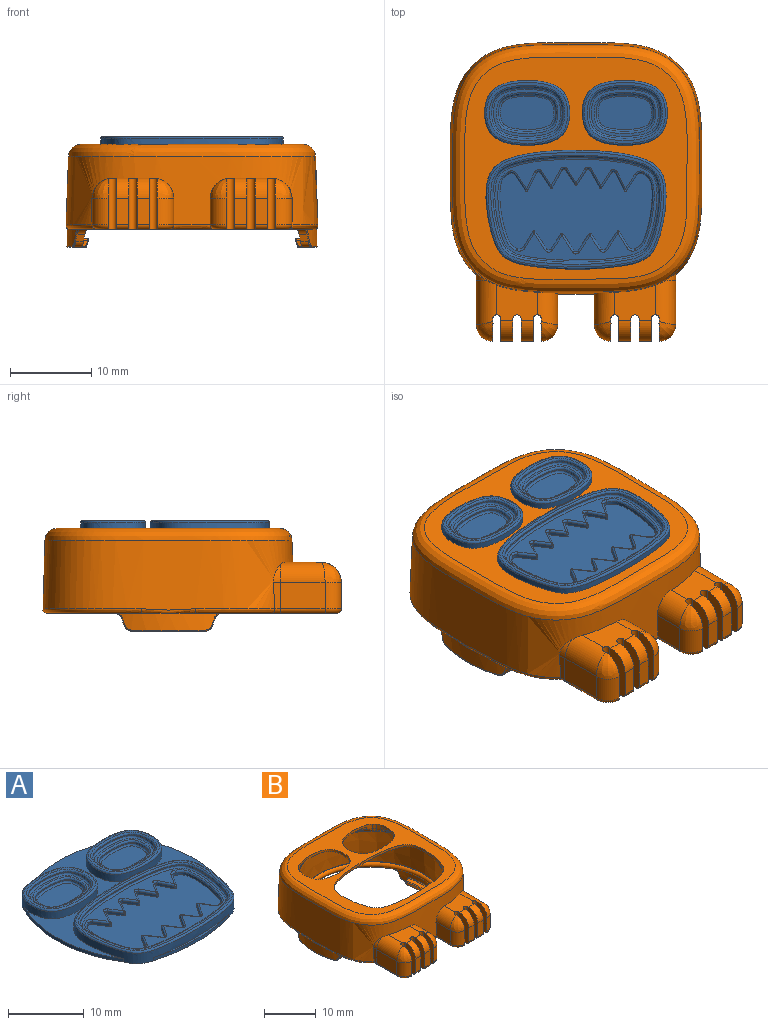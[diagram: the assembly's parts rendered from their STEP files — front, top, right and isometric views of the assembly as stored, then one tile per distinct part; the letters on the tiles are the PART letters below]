
ASSEMBLY  parts=2 mates=1
PART A: 119 faces, bbox 25.6x25.6x2.2 mm
  f0: plane 21.64x14.15mm, normal (0,0,1), area 21.1mm2, adj f114,f116
  f1: plane 9.97x7.48mm, normal (0,0,1), area 9.6mm2, adj f27,f29
  f2: plane 9.97x7.48mm, normal (0,0,1), area 9.6mm2, adj f25,f30
  f3: cylinder r=17.94mm len=17.52mm, axis (0,0,-1), area 9.2mm2, adj f6,f7,f8,f12
  f4: cylinder r=17.8mm len=18mm, axis (0,0,-1), area 9.4mm2, adj f6,f7,f11,f12
  f5: cylinder r=17.94mm len=17.52mm, axis (0,0,-1), area 9.2mm2, adj f6,f7,f8,f11
  f6: plane 25.63x22.38mm, normal (0,0,1), area 121.4mm2, adj f3,f4,f5,f8,f11,f12
  f7: plane 25.63x25.59mm, normal (0,0,-1), area 546.4mm2, adj f3,f4,f5,f8,f9,f11,f12,f117
  f8: extruded ~22.13x14.64mm, area 79.2mm2, adj f3,f5,f6,f7,f9,f10,f116
  f9: cylinder r=24.02mm len=14.06mm, axis (0,0,-1), area 7.1mm2, adj f7,f8,f10
  f10: plane 14.76x1.4mm, normal (0,0,1), area 3.3mm2, adj f8,f9
  f11: extruded ~10.45x7.96mm, area 37.8mm2, adj f4,f5,f6,f7,f29
  f12: extruded ~10.46x7.97mm, area 37.7mm2, adj f3,f4,f6,f7,f30
  f13: extruded ~8.77x6.28mm, area 3.7mm2, adj f25,f26
  f14: plane 8.27x5.78mm, normal (0,0,1), area 7.8mm2, adj f21,f26
  f15: extruded ~8.77x6.28mm, area 3.7mm2, adj f27,f28
  f16: plane 8.27x5.78mm, normal (0,0,1), area 7.8mm2, adj f22,f28
  f17: extruded ~7.07x4.58mm, area 2.9mm2, adj f22,f24
  f18: plane 6.57x4.08mm, normal (0,0,1), area 23.2mm2, adj f24
  f19: extruded ~7.07x4.58mm, area 2.9mm2, adj f21,f23
  f20: plane 6.57x4.08mm, normal (0,0,1), area 23.2mm2, adj f23
  f21: bspline ~7.57x5.09mm, area 7.9mm2, adj f14,f19
  f22: bspline ~7.57x5.09mm, area 7.9mm2, adj f16,f17
  f23: bspline ~7.07x4.59mm, area 7.5mm2, adj f19,f20
  f24: bspline ~7.07x4.59mm, area 7.5mm2, adj f17,f18
  f25: bspline ~9.27x6.78mm, area 10mm2, adj f2,f13
  f26: bspline ~8.77x6.29mm, area 9.6mm2, adj f13,f14
  f27: bspline ~9.27x6.78mm, area 10mm2, adj f1,f15
  f28: bspline ~8.77x6.29mm, area 9.6mm2, adj f15,f16
  f29: bspline ~10.47x7.98mm, area 11.6mm2, adj f1,f11
  f30: bspline ~10.47x7.98mm, area 11.6mm2, adj f2,f12
  f31: extruded ~20.4x12.91mm, area 8.6mm2, adj f114,f115
  f32: plane 19.94x12.45mm, normal (0,0,1), area 60.1mm2, adj f75,f76,f77,f78,f79,f80,f82,f83
  f33: plane 18.75x10.19mm, normal (0,0,1), area 141mm2, adj f34,f35,f36,f37,f38,f39,f40,f41
  f34: cylinder r=0.15mm len=0.4mm, axis (0,0,1), area 0.1mm2, adj f33,f35,f73,f102
  f35: plane 1.92x1.29mm, normal (-0.83,0.56,0), area 0.9mm2, adj f33,f34,f36,f104
  f36: cylinder r=0.25mm len=0.41mm, axis (0,0,1), area 0.2mm2, adj f33,f35,f37,f106
  f37: plane 2.21x1.5mm, normal (0.83,0.56,0), area 1.1mm2, adj f33,f36,f38,f108
  f38: cylinder r=0.15mm len=0.4mm, axis (0,0,1), area 0.1mm2, adj f33,f37,f39,f110
  f39: plane 1.89x1.14mm, normal (-0.86,0.52,0), area 0.9mm2, adj f33,f38,f41,f112
  f40: extruded ~9.27x2.15mm, area 4.1mm2, adj f33,f41,f42,f111
  f41: cylinder r=0.69mm len=0.78mm, axis (0,0,1), area 0.4mm2, adj f33,f39,f40,f113
  f42: cylinder r=0.5mm len=0.64mm, axis (0,0,1), area 0.3mm2, adj f33,f40,f43,f109
  f43: plane 1.98x1.32mm, normal (-0.83,-0.55,0), area 1mm2, adj f33,f42,f44,f107
  f44: cylinder r=0.15mm len=0.4mm, axis (0,0,1), area 0.1mm2, adj f33,f43,f45,f105
  f45: plane 2.23x1.11mm, normal (0.89,-0.45,0), area 1mm2, adj f33,f44,f46,f103
  f46: cylinder r=0.25mm len=0.43mm, axis (0,0,1), area 0.2mm2, adj f33,f45,f47,f101
  f47: plane 1.89x1.23mm, normal (-0.84,-0.55,0), area 0.9mm2, adj f33,f46,f48,f99
  f48: cylinder r=0.15mm len=0.4mm, axis (0,0,1), area 0.1mm2, adj f33,f47,f49,f97
  f49: plane 2.17x1.2mm, normal (0.88,-0.48,0), area 1mm2, adj f33,f48,f50,f95
  f50: cylinder r=0.25mm len=0.43mm, axis (0,0,1), area 0.2mm2, adj f33,f49,f51,f93
  f51: plane 1.81x1.16mm, normal (-0.84,-0.54,0), area 0.9mm2, adj f33,f50,f52,f91
  f52: cylinder r=0.15mm len=0.4mm, axis (0,0,1), area 0.1mm2, adj f33,f51,f53,f89
  f53: plane 1.81x1.16mm, normal (0.84,-0.54,0), area 0.9mm2, adj f33,f52,f54,f87
  f54: cylinder r=0.25mm len=0.43mm, axis (0,0,1), area 0.2mm2, adj f33,f53,f55,f85
  f55: plane 2.17x1.2mm, normal (-0.88,-0.48,0), area 1mm2, adj f33,f54,f56,f83
  f56: cylinder r=0.15mm len=0.4mm, axis (0,0,1), area 0.1mm2, adj f33,f55,f57,f81
  f57: plane 1.89x1.23mm, normal (0.84,-0.55,0), area 0.9mm2, adj f33,f56,f58,f79
  f58: cylinder r=0.25mm len=0.43mm, axis (0,0,1), area 0.2mm2, adj f33,f57,f59,f77
  f59: plane 2.23x1.11mm, normal (-0.89,-0.45,0), area 1mm2, adj f33,f58,f60,f75
  f60: cylinder r=0.15mm len=0.4mm, axis (0,0,1), area 0.1mm2, adj f33,f59,f61,f74
  f61: plane 1.97x1.31mm, normal (0.83,-0.55,0), area 0.9mm2, adj f33,f60,f63,f76
  f62: extruded ~9.26x2.15mm, area 4.1mm2, adj f33,f63,f64,f80
  f63: cylinder r=0.52mm len=0.67mm, axis (0,0,1), area 0.3mm2, adj f33,f61,f62,f78
  f64: cylinder r=0.69mm len=0.78mm, axis (0,0,1), area 0.4mm2, adj f33,f62,f65,f82
  f65: plane 1.89x1.14mm, normal (0.86,0.52,0), area 0.9mm2, adj f33,f64,f66,f84
  f66: cylinder r=0.15mm len=0.4mm, axis (0,0,1), area 0.1mm2, adj f33,f65,f67,f86
  f67: plane 2.21x1.5mm, normal (-0.83,0.56,0), area 1.1mm2, adj f33,f66,f68,f88
  f68: cylinder r=0.25mm len=0.41mm, axis (0,0,1), area 0.2mm2, adj f33,f67,f69,f90
  f69: plane 1.92x1.29mm, normal (0.83,0.56,0), area 0.9mm2, adj f33,f68,f70,f92
  f70: cylinder r=0.15mm len=0.4mm, axis (0,0,1), area 0.1mm2, adj f33,f69,f71,f94
  f71: plane 2.15x1.43mm, normal (-0.83,0.55,0), area 1mm2, adj f33,f70,f72,f96
  f72: cylinder r=0.21mm len=0.4mm, axis (0,0,1), area 0.2mm2, adj f33,f71,f73,f98
  f73: plane 2.15x1.43mm, normal (0.83,0.55,0), area 1mm2, adj f33,f34,f72,f100
  f74: bspline ~0.5x0.27mm, area 0.1mm2, adj f60,f75,f76
  f75: cylinder r=0.25mm len=2.34mm, axis (0.45,-0.89,0), area 0.9mm2, adj f32,f59,f74,f77
  f76: cylinder r=0.25mm len=2.11mm, axis (0.55,0.83,0), area 0.9mm2, adj f32,f61,f74,f78
  f77: torus R=0.5mm, axis (0,0,1), area 0.3mm2, adj f32,f58,f75,f79
  f78: torus R=0.77mm, axis (0,0,1), area 0.3mm2, adj f32,f63,f76,f80
  f79: cylinder r=0.25mm len=2.02mm, axis (0.55,0.84,0), area 0.9mm2, adj f32,f57,f77,f81
  f80: bspline ~10.14x2.62mm, area 4.1mm2, adj f32,f62,f78,f82
  f81: bspline ~0.49x0.27mm, area 0.1mm2, adj f56,f79,f83
  f82: torus R=0.94mm, axis (0,0,1), area 0.4mm2, adj f32,f64,f80,f84
  f83: cylinder r=0.25mm len=2.29mm, axis (0.48,-0.88,0), area 0.9mm2, adj f32,f55,f81,f85
  f84: cylinder r=0.25mm len=2.02mm, axis (-0.52,0.86,0), area 0.8mm2, adj f32,f65,f82,f86
  f85: torus R=0.5mm, axis (0,0,1), area 0.3mm2, adj f32,f54,f83,f87
  f86: bspline ~0.46x0.27mm, area 0.1mm2, adj f66,f84,f88
  f87: cylinder r=0.25mm len=1.94mm, axis (0.54,0.84,0), area 0.8mm2, adj f32,f53,f85,f89
  f88: cylinder r=0.25mm len=2.35mm, axis (-0.56,-0.83,0), area 1mm2, adj f32,f67,f86,f90
  f89: bspline ~0.46x0.27mm, area 0.1mm2, adj f52,f87,f91
  f90: torus R=0.5mm, axis (0,0,1), area 0.3mm2, adj f32,f68,f88,f92
  f91: cylinder r=0.25mm len=1.94mm, axis (0.54,-0.84,0), area 0.8mm2, adj f32,f51,f89,f93
  f92: cylinder r=0.25mm len=2.06mm, axis (-0.56,0.83,0), area 0.9mm2, adj f32,f69,f90,f94
  f93: torus R=0.5mm, axis (0,0,1), area 0.3mm2, adj f32,f50,f91,f95
  f94: bspline ~0.45x0.27mm, area 0.1mm2, adj f70,f92,f96
  f95: cylinder r=0.25mm len=2.29mm, axis (0.48,0.88,0), area 0.9mm2, adj f32,f49,f93,f97
  f96: cylinder r=0.25mm len=2.29mm, axis (-0.55,-0.83,0), area 1mm2, adj f32,f71,f94,f98
  f97: bspline ~0.49x0.27mm, area 0.1mm2, adj f48,f95,f99
  f98: torus R=0.46mm, axis (0,0,1), area 0.2mm2, adj f32,f72,f96,f100
  f99: cylinder r=0.25mm len=2.02mm, axis (0.55,-0.84,0), area 0.9mm2, adj f32,f47,f97,f101
  f100: cylinder r=0.25mm len=2.29mm, axis (-0.55,0.83,0), area 1mm2, adj f32,f73,f98,f102
  f101: torus R=0.5mm, axis (0,0,1), area 0.3mm2, adj f32,f46,f99,f103
  f102: bspline ~0.45x0.27mm, area 0.1mm2, adj f34,f100,f104
  f103: cylinder r=0.25mm len=2.34mm, axis (0.45,0.89,0), area 0.9mm2, adj f32,f45,f101,f105
  f104: cylinder r=0.25mm len=2.06mm, axis (-0.56,-0.83,0), area 0.9mm2, adj f32,f35,f102,f106
  f105: bspline ~0.5x0.27mm, area 0.1mm2, adj f44,f103,f107
  f106: torus R=0.5mm, axis (0,0,1), area 0.3mm2, adj f32,f36,f104,f108
  f107: cylinder r=0.25mm len=2.12mm, axis (0.55,-0.83,0), area 0.9mm2, adj f32,f43,f105,f109
  f108: cylinder r=0.25mm len=2.35mm, axis (-0.56,0.83,0), area 1mm2, adj f32,f37,f106,f110
  f109: torus R=0.75mm, axis (0,0,1), area 0.3mm2, adj f32,f42,f107,f111
  f110: bspline ~0.46x0.27mm, area 0.1mm2, adj f38,f108,f112
  f111: bspline ~10.15x2.61mm, area 4.2mm2, adj f32,f40,f109,f113
  f112: cylinder r=0.25mm len=2.02mm, axis (-0.52,-0.86,0), area 0.8mm2, adj f32,f39,f110,f113
  f113: torus R=0.94mm, axis (0,0,1), area 0.4mm2, adj f32,f41,f111,f112
  f114: bspline ~20.94x13.45mm, area 22.7mm2, adj f0,f31
  f115: bspline ~20.44x12.95mm, area 22.3mm2, adj f31,f32
  f116: bspline ~22.14x14.65mm, area 24.4mm2, adj f0,f8
  f117: cone r=1.05mm half-angle=2deg, axis (0,0,1), area 1.3mm2, adj f7,f118
  f118: plane 2.09x2.09mm, normal (0,0,-1), area 3.4mm2, adj f117
PART B: 284 faces, bbox 35.3x39.1x19.3 mm
  f0: plane 30.01x17.46mm, normal (0,0,-1), area 97.2mm2, adj f13,f14,f15,f18,f19,f29,f37,f40
  f1: plane 5.21x4.6mm, normal (0,0,1), area 17.8mm2, adj f8,f9,f11,f17,f156,f230,f231,f232
  f2: plane 3.25x1.5mm, normal (0,-1,0), area 4.9mm2, adj f8,f13,f231,f235
  f3: plane 3.25x1.5mm, normal (0,-1,0), area 4.9mm2, adj f9,f14,f232,f237
  f4: plane 5.19x4.58mm, normal (0,0,1), area 17.8mm2, adj f12,f17,f158,f160,f162,f220,f221,f223
  f5: plane 3.25x1.5mm, normal (0,-1,0), area 4.9mm2, adj f160,f174,f225,f227
  f6: plane 3.25x1.5mm, normal (0,-1,0), area 4.9mm2, adj f12,f15,f220,f224
  f7: bspline ~2.64x2.42mm, area 5.1mm2, adj f152,f156,f234
  f8: cylinder r=2.5mm len=2.5mm, axis (1,0,0), area 5.9mm2, adj f1,f2,f231,f235
  f9: cylinder r=2.5mm len=2.5mm, axis (1,0,0), area 5.9mm2, adj f1,f3,f232,f237
  f10: bspline ~2.64x2.42mm, area 5.1mm2, adj f11,f153,f229
  f11: cylinder r=2.5mm len=5.49mm, axis (0,-1,0), area 19.9mm2, adj f1,f10,f17,f148,f157,f229,f230
  f12: cylinder r=2.5mm len=2.5mm, axis (1,0,0), area 5.9mm2, adj f4,f6,f220,f224
  f13: cylinder r=0.5mm len=1.5mm, axis (1,0,0), area 1.2mm2, adj f0,f2,f231,f235
  f14: cylinder r=0.5mm len=1.5mm, axis (1,0,0), area 1.2mm2, adj f0,f3,f232,f237
  f15: cylinder r=0.5mm len=1.5mm, axis (1,0,0), area 1.2mm2, adj f0,f6,f220,f224
  f16: plane 30.01x11.69mm, normal (0,0,-1), area 44.9mm2, adj f18,f19,f29,f36,f41,f175,f188,f189
  f17: bspline ~30.97x30.97mm, area 781mm2, adj f1,f4,f11,f146,f147,f149,f150,f156
  f18: cone r=15.12mm half-angle=2deg, axis (0,0,-1), area 23.5mm2, adj f0,f16,f173,f182,f183,f184,f185,f186
  f19: cone r=15.12mm half-angle=2deg, axis (0,0,-1), area 23.5mm2, adj f0,f16,f177,f189,f190,f191,f192,f193
  f20: plane 13.19x2.44mm, normal (0,0,-1), area 4.6mm2, adj f102,f113
  f21: plane 13.37x1.8mm, normal (0,0,-1), area 4.6mm2, adj f103,f114
  f22: plane 13.19x2.44mm, normal (0,0,-1), area 4.6mm2, adj f100,f115
  f23: plane 10.51x1.08mm, normal (0,0,-1), area 3.6mm2, adj f101,f107
  f24: extruded ~10.44x7.96mm, area 17.2mm2, adj f28,f95,f96,f102,f103,f111,f112,f113
  f25: extruded ~10.44x7.96mm, area 17.2mm2, adj f28,f95,f97,f100,f103,f108,f114,f115
  f26: extruded ~22.12x13.12mm, area 25.1mm2, adj f28,f95,f98,f99,f100,f102,f109,f110
  f27: extruded ~17.62x1.72mm, area 11.5mm2, adj f28,f95,f98,f99,f101,f104,f105,f106
  f28: plane 27.38x27.38mm, normal (0,0,1), area 268.4mm2, adj f24,f25,f26,f27,f96,f97,f98,f99
  f29: cone r=14.12mm half-angle=2deg, axis (0,0,-1), area 59.9mm2, adj f0,f16,f30,f31,f32,f33,f34,f35
  f30: plane 1.15x0.94mm, normal (0,-0.94,-0.34), area 1mm2, adj f29,f40,f42,f183
  f31: plane 1.15x0.94mm, normal (0,0.94,-0.34), area 1mm2, adj f29,f41,f43,f187
  f32: plane 9x1.6mm, normal (0,0,-1), area 7.6mm2, adj f29,f42,f43,f45,f62,f85,f185
  f33: plane 1.15x0.94mm, normal (0,-0.94,-0.34), area 1mm2, adj f29,f37,f39,f194
  f34: plane 1.15x0.94mm, normal (0,0.94,-0.34), area 1mm2, adj f29,f36,f38,f190
  f35: plane 9x1.6mm, normal (0,0,-1), area 7.6mm2, adj f29,f38,f39,f51,f67,f84,f192
  f36: cylinder r=1mm len=1.46mm, axis (1,0,0), area 1.2mm2, adj f16,f29,f34,f189
  f37: cylinder r=1mm len=1.46mm, axis (1,0,0), area 1.2mm2, adj f0,f29,f33,f195
  f38: cylinder r=1mm len=1.25mm, axis (1,0,0), area 1.1mm2, adj f29,f34,f35,f191
  f39: cylinder r=1mm len=1.25mm, axis (1,0,0), area 1.1mm2, adj f29,f33,f35,f193
  f40: cylinder r=1mm len=1.46mm, axis (-1,0,0), area 1.2mm2, adj f0,f29,f30,f182
  f41: cylinder r=1mm len=1.46mm, axis (-1,0,0), area 1.2mm2, adj f16,f29,f31,f188
  f42: cylinder r=1mm len=1.25mm, axis (-1,0,0), area 1.1mm2, adj f29,f30,f32,f184
  f43: cylinder r=1mm len=1.25mm, axis (-1,0,0), area 1.1mm2, adj f29,f31,f32,f186
  f44: plane 7.08x1.39mm, normal (0,0,1), area 6.7mm2, adj f54,f55,f56,f88
  f45: plane 7.53x1.37mm, normal (0,0,-1), area 6.3mm2, adj f32,f59,f62,f65,f91
  f46: cone r=13.04mm half-angle=20.9deg, axis (0,0,-1), area 5.3mm2, adj f55,f60,f61,f65
  f47: plane 0.98x0.75mm, normal (0.26,-0.97,0), area 0.6mm2, adj f54,f59,f60,f90
  f48: plane 0.98x0.75mm, normal (0.26,0.97,0), area 0.6mm2, adj f56,f61,f62,f86
  f49: plane 7.08x1.39mm, normal (0,0,1), area 6.7mm2, adj f72,f73,f77,f81
  f50: cone r=13.04mm half-angle=20.9deg, axis (0,0,-1), area 5.3mm2, adj f68,f71,f74,f77
  f51: plane 7.53x1.37mm, normal (0,0,-1), area 6.3mm2, adj f35,f66,f67,f68,f78
  f52: plane 0.98x0.75mm, normal (-0.26,0.97,0), area 0.6mm2, adj f66,f71,f72,f79
  f53: plane 0.98x0.75mm, normal (-0.26,-0.97,0), area 0.6mm2, adj f67,f73,f74,f83
  f54: cylinder r=0.15mm len=0.99mm, axis (0.97,0.26,0), area 0.2mm2, adj f44,f47,f57,f89
  f55: torus R=13.26mm, axis (0,0,1), area 1.9mm2, adj f44,f46,f57,f58
  f56: cylinder r=0.15mm len=0.99mm, axis (-0.97,0.26,0), area 0.2mm2, adj f44,f48,f58,f87
  f57: sphere r=0.15mm, area 0.1mm2, adj f54,f55,f60
  f58: sphere r=0.15mm, area 0mm2, adj f55,f56,f61
  f59: cylinder r=0.15mm len=0.75mm, axis (-0.97,-0.26,0), area 0.2mm2, adj f45,f47,f63,f91
  f60: bspline ~10.55x4mm, area 0.2mm2, adj f46,f47,f57,f63
  f61: bspline ~10.55x4mm, area 0.2mm2, adj f46,f48,f58,f64
  f62: cylinder r=0.15mm len=0.9mm, axis (0.97,-0.26,0), area 0.2mm2, adj f32,f45,f48,f64,f85
  f63: sphere r=0.15mm, area 0mm2, adj f59,f60,f65
  f64: sphere r=0.15mm, area 0mm2, adj f61,f62,f65
  f65: torus R=13.55mm, axis (0,0,-1), area 1.2mm2, adj f45,f46,f63,f64
  f66: cylinder r=0.15mm len=0.75mm, axis (-0.97,-0.26,0), area 0.2mm2, adj f51,f52,f69,f78
  f67: cylinder r=0.15mm len=0.9mm, axis (0.97,-0.26,0), area 0.2mm2, adj f35,f51,f53,f70,f84
  f68: torus R=13.55mm, axis (0,0,-1), area 1.2mm2, adj f50,f51,f69,f70
  f69: sphere r=0.15mm, area 0mm2, adj f66,f68,f71
  f70: sphere r=0.15mm, area 0mm2, adj f67,f68,f74
  f71: bspline ~10.55x4mm, area 0.2mm2, adj f50,f52,f69,f75
  f72: cylinder r=0.15mm len=0.99mm, axis (0.97,0.26,0), area 0.2mm2, adj f49,f52,f75,f80
  f73: cylinder r=0.15mm len=0.99mm, axis (-0.97,0.26,0), area 0.2mm2, adj f49,f53,f76,f82
  f74: bspline ~10.55x4mm, area 0.2mm2, adj f50,f53,f70,f76
  f75: sphere r=0.15mm, area 0.1mm2, adj f71,f72,f77
  f76: sphere r=0.15mm, area 0mm2, adj f73,f74,f77
  f77: torus R=13.26mm, axis (0,0,1), area 1.9mm2, adj f49,f50,f75,f76
  f78: bspline ~0.35x0.34mm, area 0mm2, adj f29,f51,f66,f79
  f79: bspline ~3.76x0.27mm, area 0.2mm2, adj f29,f52,f78,f80
  f80: bspline ~0.37x0.32mm, area 0.1mm2, adj f29,f72,f79,f81
  f81: torus R=14.23mm, axis (0,0,1), area 1.7mm2, adj f29,f49,f80,f82
  f82: bspline ~0.37x0.34mm, area 0.1mm2, adj f29,f73,f81,f83
  f83: bspline ~3.76x0.27mm, area 0.2mm2, adj f29,f53,f82,f84
  f84: bspline ~0.34x0.33mm, area 0mm2, adj f29,f35,f67,f83
  f85: bspline ~0.34x0.33mm, area 0mm2, adj f29,f32,f62,f86
  f86: bspline ~3.76x0.27mm, area 0.2mm2, adj f29,f48,f85,f87
  f87: bspline ~0.37x0.34mm, area 0.1mm2, adj f29,f56,f86,f88
  f88: torus R=14.23mm, axis (0,0,1), area 1.7mm2, adj f29,f44,f87,f89
  f89: bspline ~0.37x0.32mm, area 0.1mm2, adj f29,f54,f88,f90
  f90: bspline ~3.76x0.27mm, area 0.2mm2, adj f29,f47,f89,f91
  f91: bspline ~0.35x0.34mm, area 0mm2, adj f29,f45,f59,f90
  f92: plane 28.67x28.67mm, normal (0,0,-1), area 11mm2, adj f29,f94
  f93: plane 28.6x28.6mm, normal (0,0,1), area 7.6mm2, adj f94,f95
  f94: torus R=14.21mm, axis (0,0,-1), area 150.5mm2, adj f92,f93
  f95: cone r=14.12mm half-angle=2deg, axis (0,0,-1), area 651mm2, adj f24,f25,f26,f27,f93,f96,f97,f98
  f96: cylinder r=14.02mm len=1mm, axis (0,0,-1), area 0.8mm2, adj f24,f28,f95
  f97: cylinder r=14.02mm len=1mm, axis (0,0,-1), area 0.8mm2, adj f25,f28,f95
  f98: cylinder r=14.02mm len=1mm, axis (0,0,-1), area 0.9mm2, adj f26,f27,f28,f95
  f99: cylinder r=14.02mm len=1mm, axis (0,0,-1), area 0.9mm2, adj f26,f27,f28,f95
  f100: torus R=13.29mm, axis (0,0,1), area 22.9mm2, adj f22,f25,f26,f95,f108,f109
  f101: torus R=13.29mm, axis (0,0,1), area 17.8mm2, adj f23,f27,f95,f105,f106
  f102: torus R=13.29mm, axis (0,0,1), area 22.9mm2, adj f20,f24,f26,f95,f110,f111
  f103: torus R=13.29mm, axis (0,0,1), area 23.4mm2, adj f21,f24,f25,f95,f112,f117
  f104: plane 14.76x1.4mm, normal (0,0,-1), area 3.3mm2, adj f27,f107
  f105: plane 1.78x0.48mm, normal (0,0,1), area 0.1mm2, adj f27,f101,f107
  f106: plane 1.78x0.48mm, normal (0,0,1), area 0.1mm2, adj f27,f101,f107
  f107: cylinder r=24.02mm len=14.06mm, axis (0,0,-1), area 7.1mm2, adj f23,f27,f104,f105,f106
  f108: plane 2.85x1.11mm, normal (0,0,1), area 0.4mm2, adj f25,f100,f115
  f109: plane 1.49x0.85mm, normal (0,0,1), area 0.1mm2, adj f26,f100,f115
  f110: plane 1.49x0.85mm, normal (0,0,1), area 0.1mm2, adj f26,f102,f113
  f111: plane 2.85x1.11mm, normal (0,0,1), area 0.4mm2, adj f24,f102,f113
  f112: plane 2.32x1.14mm, normal (0,0,1), area 0.3mm2, adj f24,f103,f114
  f113: cylinder r=17.94mm len=17.52mm, axis (0,0,-1), area 9.2mm2, adj f20,f24,f26,f110,f111,f116
  f114: cylinder r=17.8mm len=18mm, axis (0,0,-1), area 9.4mm2, adj f21,f24,f25,f112,f116,f117
  f115: cylinder r=17.94mm len=17.52mm, axis (0,0,-1), area 9.2mm2, adj f22,f25,f26,f108,f109,f116
  f116: plane 25.63x22.38mm, normal (0,0,-1), area 121.4mm2, adj f24,f25,f26,f113,f114,f115
  f117: plane 2.32x1.14mm, normal (0,0,1), area 0.3mm2, adj f25,f103,f114
  f118: plane 6.7x6.7mm, normal (0,0,-1), area 12mm2, adj f119,f120,f121,f122,f123,f124
  f119: plane 9.26x1.21mm, normal (0.05,1,-0.03), area 9.1mm2, adj f118,f120,f124,f218
  f120: bspline ~9.26x0.79mm, area 7.5mm2, adj f118,f119,f121,f216
  f121: bspline ~9.25x6.17mm, area 78.7mm2, adj f118,f120,f122,f214
  f122: bspline ~9.26x0.79mm, area 7.5mm2, adj f118,f121,f123,f215
  f123: plane 9.26x1.21mm, normal (1,0.05,-0.03), area 9.1mm2, adj f118,f122,f124,f217
  f124: bspline ~9.41x5.65mm, area 73.1mm2, adj f118,f119,f123,f217,f218,f219
  f125: plane 6.7x6.7mm, normal (0,0,-1), area 12mm2, adj f126,f127,f128,f129,f130,f131
  f126: bspline ~9.41x5.65mm, area 73.1mm2, adj f125,f127,f131,f210,f212,f213
  f127: plane 9.26x1.2mm, normal (-0.05,-1,-0.03), area 9mm2, adj f125,f126,f128,f210
  f128: bspline ~9.26x0.79mm, area 7.5mm2, adj f125,f127,f129,f208
  f129: bspline ~9.41x6.17mm, area 78.7mm2, adj f125,f128,f130,f209
  f130: bspline ~9.26x0.79mm, area 7.5mm2, adj f125,f129,f131,f211
  f131: plane 9.26x1.2mm, normal (-1,-0.05,-0.03), area 9mm2, adj f125,f126,f130,f213
  f132: plane 6.7x6.7mm, normal (0,0,-1), area 12mm2, adj f133,f134,f135,f136,f137,f138
  f133: bspline ~9.41x5.65mm, area 73.1mm2, adj f132,f134,f138,f204,f206,f207
  f134: plane 9.26x1.21mm, normal (1,-0.05,-0.03), area 9.1mm2, adj f132,f133,f135,f204
  f135: bspline ~9.26x0.79mm, area 7.5mm2, adj f132,f134,f136,f202
  f136: bspline ~9.25x6.17mm, area 78.7mm2, adj f132,f135,f137,f203
  f137: bspline ~9.26x0.79mm, area 7.5mm2, adj f132,f136,f138,f205
  f138: plane 9.26x1.2mm, normal (0.05,-1,-0.03), area 9mm2, adj f132,f133,f137,f207
  f139: plane 6.7x6.7mm, normal (0,0,-1), area 12mm2, adj f140,f141,f142,f143,f144,f145
  f140: bspline ~9.41x5.65mm, area 73.1mm2, adj f139,f141,f145,f198,f200,f201
  f141: plane 9.26x1.2mm, normal (-1,0.05,-0.03), area 9mm2, adj f139,f140,f142,f198
  f142: bspline ~9.26x0.79mm, area 7.5mm2, adj f139,f141,f143,f196
  f143: bspline ~9.25x6.17mm, area 78.7mm2, adj f139,f142,f144,f197
  f144: bspline ~9.26x0.79mm, area 7.5mm2, adj f139,f143,f145,f199
  f145: plane 9.26x1.21mm, normal (-0.05,1,-0.03), area 9.1mm2, adj f139,f140,f144,f201
  f146: plane 3.88x3.25mm, normal (1,0,0), area 12.4mm2, adj f17,f152,f156,f166,f168
  f147: plane 3.25x0.89mm, normal (-1,-0.06,0), area 2.6mm2, adj f17,f148,f157,f169,f171
  f148: plane 5.46x3.25mm, normal (-1,0,0), area 17.7mm2, adj f11,f147,f153,f167
  f149: plane 3.88x3.25mm, normal (-1,0,0), area 12.4mm2, adj f17,f154,f158,f168,f170
  f150: plane 3.25x0.89mm, normal (1,-0.06,0), area 2.6mm2, adj f17,f151,f163,f179,f180
  f151: plane 5.46x3.25mm, normal (1,0,0), area 17.7mm2, adj f150,f155,f162,f178
  f152: cylinder r=2mm len=3.25mm, axis (0,0,-1), area 10.2mm2, adj f7,f146,f164,f234
  f153: cylinder r=2mm len=3.25mm, axis (0,0,1), area 10.2mm2, adj f10,f148,f165,f229
  f154: cylinder r=2mm len=3.25mm, axis (0,0,-1), area 10.2mm2, adj f149,f159,f172,f228
  f155: cylinder r=2mm len=3.25mm, axis (0,0,1), area 10.2mm2, adj f151,f161,f176,f222
  f156: cylinder r=2.5mm len=4.02mm, axis (0,1,0), area 14.3mm2, adj f1,f7,f17,f146,f233,f234
  f157: cylinder r=2.5mm len=2.16mm, axis (0.06,-1,0), area 1.2mm2, adj f11,f17,f147
  f158: cylinder r=2.5mm len=4.02mm, axis (0,-1,0), area 14.3mm2, adj f4,f17,f149,f159,f226,f228
  f159: bspline ~2.64x2.42mm, area 5.1mm2, adj f154,f158,f228
  f160: cylinder r=2.5mm len=2.5mm, axis (1,0,0), area 5.9mm2, adj f4,f5,f225,f227
  f161: bspline ~2.64x2.42mm, area 5.1mm2, adj f155,f162,f222
  f162: cylinder r=2.5mm len=5.49mm, axis (0,1,0), area 19.9mm2, adj f4,f17,f151,f161,f163,f221,f222
  f163: cylinder r=2.5mm len=2.16mm, axis (0.06,1,0), area 1.2mm2, adj f17,f150,f162
  f164: torus R=1.5mm, axis (0,0,1), area 2.2mm2, adj f0,f152,f166,f234
  f165: torus R=1.5mm, axis (0,0,1), area 2.2mm2, adj f0,f153,f167,f229
  f166: cylinder r=0.5mm len=4.27mm, axis (0,1,0), area 3.2mm2, adj f0,f146,f164,f168
  f167: cylinder r=0.5mm len=5.47mm, axis (0,-1,0), area 4.3mm2, adj f0,f148,f165,f169
  f168: bspline ~8.83x0.56mm, area 3.9mm2, adj f0,f17,f146,f149,f166,f170
  f169: cylinder r=0.5mm len=0.98mm, axis (0.06,-1,0), area 0.7mm2, adj f0,f147,f167,f171
  f170: cylinder r=0.5mm len=4.27mm, axis (0,-1,0), area 3.2mm2, adj f0,f149,f168,f172
  f171: bspline ~11.53x4.15mm, area 8.4mm2, adj f0,f17,f147,f169,f173
  f172: torus R=1.5mm, axis (0,0,1), area 2.2mm2, adj f0,f154,f170,f228
  f173: bspline ~7.19x0.59mm, area 3.7mm2, adj f17,f18,f171,f175
  f174: cylinder r=0.5mm len=1.5mm, axis (1,0,0), area 1.2mm2, adj f0,f5,f225,f227
  f175: bspline ~31.01x13.8mm, area 37.1mm2, adj f16,f17,f173,f177
  f176: torus R=1.5mm, axis (0,0,1), area 2.2mm2, adj f0,f155,f178,f222
  f177: bspline ~7.19x0.59mm, area 3.7mm2, adj f17,f19,f175,f179
  f178: cylinder r=0.5mm len=5.47mm, axis (0,1,0), area 4.3mm2, adj f0,f151,f176,f180
  f179: bspline ~11.84x4.86mm, area 8.4mm2, adj f0,f17,f150,f177,f180
  f180: cylinder r=0.5mm len=0.98mm, axis (0.06,1,0), area 0.7mm2, adj f0,f150,f178,f179
  f181: bspline ~30.38x30.38mm, area 234.3mm2, adj f17,f28
  f182: bspline ~1.36x1.02mm, area 0.2mm2, adj f0,f18,f40,f183
  f183: bspline ~8.6x3.22mm, area 0.2mm2, adj f18,f30,f182,f184
  f184: bspline ~1.22x0.89mm, area 0.3mm2, adj f18,f42,f183,f185
  f185: torus R=15.27mm, axis (0,0,-1), area 2.2mm2, adj f18,f32,f184,f186
  f186: bspline ~1.19x0.76mm, area 0.3mm2, adj f18,f43,f185,f187
  f187: bspline ~8.6x3.22mm, area 0.2mm2, adj f18,f31,f186,f188
  f188: bspline ~1.36x1.02mm, area 0.2mm2, adj f16,f18,f41,f187
  f189: bspline ~1.36x1.02mm, area 0.2mm2, adj f16,f19,f36,f190
  f190: bspline ~8.6x3.22mm, area 0.2mm2, adj f19,f34,f189,f191
  f191: bspline ~1.22x0.89mm, area 0.3mm2, adj f19,f38,f190,f192
  f192: torus R=15.27mm, axis (0,0,-1), area 2.2mm2, adj f19,f35,f191,f193
  f193: bspline ~1.19x0.76mm, area 0.3mm2, adj f19,f39,f192,f194
  f194: bspline ~8.6x3.22mm, area 0.2mm2, adj f19,f33,f193,f195
  f195: bspline ~1.36x1.02mm, area 0.2mm2, adj f0,f19,f37,f194
  f196: bspline ~0.86x0.62mm, area 0.2mm2, adj f0,f142,f197,f198
  f197: bspline ~7.99x7.99mm, area 2mm2, adj f0,f143,f196,f199
  f198: cylinder r=0.15mm len=1mm, axis (0.05,1,0), area 0.2mm2, adj f0,f140,f141,f196,f200
  f199: bspline ~0.92x0.51mm, area 0.2mm2, adj f0,f144,f197,f201
  f200: bspline ~6.04x5.85mm, area 1.8mm2, adj f0,f140,f198,f201
  f201: cylinder r=0.15mm len=1mm, axis (1,0.05,0), area 0.2mm2, adj f0,f140,f145,f199,f200
  f202: bspline ~0.86x0.62mm, area 0.2mm2, adj f16,f135,f203,f204
  f203: bspline ~7.99x7.99mm, area 2mm2, adj f16,f136,f202,f205
  f204: cylinder r=0.15mm len=1mm, axis (-0.05,-1,0), area 0.2mm2, adj f16,f133,f134,f202,f206
  f205: bspline ~0.92x0.51mm, area 0.2mm2, adj f16,f137,f203,f207
  f206: bspline ~6.04x5.85mm, area 1.8mm2, adj f16,f133,f204,f207
  f207: cylinder r=0.15mm len=1mm, axis (-1,-0.05,0), area 0.2mm2, adj f16,f133,f138,f205,f206
  f208: bspline ~0.86x0.62mm, area 0.2mm2, adj f16,f128,f209,f210
  f209: bspline ~7.99x7.99mm, area 2mm2, adj f16,f129,f208,f211
  f210: cylinder r=0.15mm len=1mm, axis (-1,0.05,0), area 0.2mm2, adj f16,f126,f127,f208,f212
  f211: bspline ~0.92x0.51mm, area 0.2mm2, adj f16,f130,f209,f213
  f212: bspline ~6.04x5.85mm, area 1.8mm2, adj f16,f126,f210,f213
  f213: cylinder r=0.15mm len=1mm, axis (-0.05,1,0), area 0.2mm2, adj f16,f126,f131,f211,f212
  f214: bspline ~7.99x7.99mm, area 2mm2, adj f0,f121,f215,f216
  f215: bspline ~0.92x0.51mm, area 0.2mm2, adj f0,f122,f214,f217
  f216: bspline ~0.86x0.62mm, area 0.2mm2, adj f0,f120,f214,f218
  f217: cylinder r=0.15mm len=1mm, axis (0.05,-1,0), area 0.2mm2, adj f0,f123,f124,f215,f219
  f218: cylinder r=0.15mm len=1mm, axis (1,-0.05,0), area 0.2mm2, adj f0,f119,f124,f216,f219
  f219: bspline ~6.04x5.85mm, area 1.8mm2, adj f0,f124,f217,f218
  f220: plane 6.25x2.75mm, normal (1,0,0), area 15.8mm2, adj f0,f4,f6,f12,f15,f221
  f221: cylinder r=0.5mm len=6.25mm, axis (0,0,-1), area 9.8mm2, adj f0,f4,f162,f220,f222
  f222: plane 8.12x4.67mm, normal (-1,0,0), area 15.7mm2, adj f0,f155,f161,f162,f176,f221
  f223: cylinder r=0.5mm len=6.25mm, axis (0,0,-1), area 9.8mm2, adj f0,f4,f224,f225
  f224: plane 6.25x2.75mm, normal (-1,0,0), area 15.8mm2, adj f0,f4,f6,f12,f15,f223
  f225: plane 6.25x2.75mm, normal (1,0,0), area 15.8mm2, adj f0,f4,f5,f160,f174,f223
  f226: cylinder r=0.5mm len=6.25mm, axis (0,0,-1), area 9.8mm2, adj f0,f4,f158,f227,f228
  f227: plane 6.25x2.75mm, normal (-1,0,0), area 15.8mm2, adj f0,f4,f5,f160,f174,f226
  f228: plane 8.12x4.67mm, normal (1,0,0), area 15.7mm2, adj f0,f154,f158,f159,f172,f226
  f229: plane 8.12x4.67mm, normal (1,0,0), area 15.7mm2, adj f0,f10,f11,f153,f165,f230
  f230: cylinder r=0.5mm len=6.25mm, axis (0,0,-1), area 9.8mm2, adj f0,f1,f11,f229,f231
  f231: plane 6.25x2.75mm, normal (-1,0,0), area 15.8mm2, adj f0,f1,f2,f8,f13,f230
  f232: plane 6.25x2.75mm, normal (1,0,0), area 15.8mm2, adj f0,f1,f3,f9,f14,f233
  f233: cylinder r=0.5mm len=6.25mm, axis (0,0,-1), area 9.8mm2, adj f0,f1,f156,f232,f234
  f234: plane 8.12x4.67mm, normal (-1,0,0), area 15.7mm2, adj f0,f7,f152,f156,f164,f233
  f235: plane 6.25x2.75mm, normal (1,0,0), area 15.8mm2, adj f0,f1,f2,f8,f13,f236
  f236: cylinder r=0.5mm len=6.25mm, axis (0,0,-1), area 9.8mm2, adj f0,f1,f235,f237
  f237: plane 6.25x2.75mm, normal (-1,0,0), area 15.8mm2, adj f0,f1,f3,f9,f14,f236
  f238: cylinder r=0.15mm len=5mm, axis (0,0,-1), area 1.9mm2, adj f239,f248,f249,f276
  f239: plane 5x2.1mm, normal (1,0,0), area 10.5mm2, adj f238,f240,f249,f278
  f240: plane 6.54x5mm, normal (0.05,-1,0), area 32.7mm2, adj f239,f241,f249,f280
  f241: cylinder r=5.76mm len=5mm, axis (0,0,-1), area 7.4mm2, adj f240,f242,f249,f282
  f242: plane 5x2.69mm, normal (-1,0,0), area 13.4mm2, adj f241,f243,f249,f283
  f243: cylinder r=0.15mm len=5mm, axis (0,0,-1), area 1.9mm2, adj f242,f244,f249,f281
  f244: cylinder r=1.5mm len=5mm, axis (0,0,-1), area 13.6mm2, adj f243,f245,f249,f279
  f245: cylinder r=0.15mm len=5mm, axis (0,0,-1), area 1.3mm2, adj f244,f246,f249,f277
  f246: cylinder r=1.5mm len=5mm, axis (0,0,-1), area 12.9mm2, adj f245,f247,f249,f275
  f247: cylinder r=0.15mm len=5mm, axis (0,0,-1), area 1.3mm2, adj f246,f248,f249,f273
  f248: cylinder r=1.5mm len=5mm, axis (0,0,-1), area 13.6mm2, adj f238,f247,f249,f274
  f249: plane 8x2.84mm, normal (0,0,-1), area 15.9mm2, adj f238,f239,f240,f241,f242,f243,f244,f245
  f250: cylinder r=1.5mm len=5mm, axis (0,0,-1), area 13.6mm2, adj f251,f260,f261,f268
  f251: cylinder r=0.15mm len=5mm, axis (0,0,-1), area 1.3mm2, adj f250,f252,f261,f266
  f252: cylinder r=1.5mm len=5mm, axis (0,0,-1), area 12.9mm2, adj f251,f253,f261,f264
  f253: cylinder r=0.15mm len=5mm, axis (0,0,-1), area 1.3mm2, adj f252,f254,f261,f262
  f254: cylinder r=1.5mm len=5mm, axis (0,0,-1), area 13.6mm2, adj f253,f255,f261,f263
  f255: cylinder r=0.15mm len=5mm, axis (0,0,-1), area 1.9mm2, adj f254,f256,f261,f265
  f256: plane 5x2.69mm, normal (1,0,0), area 13.4mm2, adj f255,f257,f261,f267
  f257: cylinder r=5.76mm len=5mm, axis (0,0,-1), area 7.4mm2, adj f256,f258,f261,f269
  f258: plane 6.54x5mm, normal (-0.05,-1,0), area 32.7mm2, adj f257,f259,f261,f271
  f259: plane 5x2.1mm, normal (-1,0,0), area 10.5mm2, adj f258,f260,f261,f272
  f260: cylinder r=0.15mm len=5mm, axis (0,0,-1), area 1.9mm2, adj f250,f259,f261,f270
  f261: plane 8x2.84mm, normal (0,0,-1), area 15.9mm2, adj f250,f251,f252,f253,f254,f255,f256,f257
  f262: torus R=0.4mm, axis (0,0,1), area 0.2mm2, adj f0,f253,f263,f264
  f263: torus R=1.25mm, axis (0,0,1), area 1mm2, adj f0,f254,f262,f265
  f264: torus R=1.25mm, axis (0,0,1), area 1mm2, adj f0,f252,f262,f266
  f265: torus R=0.4mm, axis (0,0,1), area 0.2mm2, adj f0,f255,f263,f267
  f266: torus R=0.4mm, axis (0,0,1), area 0.2mm2, adj f0,f251,f264,f268
  f267: cylinder r=0.25mm len=3.04mm, axis (0,1,0), area 1.1mm2, adj f0,f256,f265,f269
  f268: torus R=1.25mm, axis (0,0,1), area 1mm2, adj f0,f250,f266,f270
  f269: torus R=5.51mm, axis (0,0,1), area 0.6mm2, adj f0,f257,f267,f271
  f270: torus R=0.4mm, axis (0,0,1), area 0.2mm2, adj f0,f260,f268,f272
  f271: cylinder r=0.25mm len=6.79mm, axis (1,-0.05,0), area 2.6mm2, adj f0,f258,f269,f272
  f272: cylinder r=0.25mm len=2.34mm, axis (0,-1,0), area 0.9mm2, adj f0,f259,f270,f271
  f273: torus R=0.4mm, axis (0,0,1), area 0.2mm2, adj f0,f247,f274,f275
  f274: torus R=1.25mm, axis (0,0,1), area 1mm2, adj f0,f248,f273,f276
  f275: torus R=1.25mm, axis (0,0,1), area 1mm2, adj f0,f246,f273,f277
  f276: torus R=0.4mm, axis (0,0,1), area 0.2mm2, adj f0,f238,f274,f278
  f277: torus R=0.4mm, axis (0,0,1), area 0.2mm2, adj f0,f245,f275,f279
  f278: cylinder r=0.25mm len=2.34mm, axis (0,1,0), area 0.9mm2, adj f0,f239,f276,f280
  f279: torus R=1.25mm, axis (0,0,1), area 1mm2, adj f0,f244,f277,f281
  f280: cylinder r=0.25mm len=6.79mm, axis (1,0.05,0), area 2.6mm2, adj f0,f240,f278,f282
  f281: torus R=0.4mm, axis (0,0,1), area 0.2mm2, adj f0,f243,f279,f283
  f282: torus R=5.51mm, axis (0,0,1), area 0.6mm2, adj f0,f241,f280,f283
  f283: cylinder r=0.25mm len=3.04mm, axis (0,-1,0), area 1.1mm2, adj f0,f242,f281,f282
PLACE A t=(0,0,10.81)mm
PLACE B at identity fixed
MATE fastened A.f6 <-> B.f116  axis (0,0,1) through (-1.69,4.07,11.32)mm
